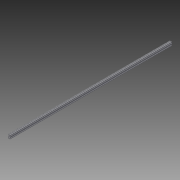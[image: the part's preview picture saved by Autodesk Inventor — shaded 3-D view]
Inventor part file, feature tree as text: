
AUTODESK INVENTOR PART (.ipt)
format: ipt  version: 2013 (Build 170138000, 138)  size: 219,648 bytes
history: native  units: in
note: dims shown in document units (in); Inventor stores cm internally (conversion verified against a paired STEP export)
features: extrude x1, sketch x1
ambient origin geometry x8: Origin, YZ Plane, XZ Plane, XY Plane, X Axis, Y Axis, Z Axis, Center Point
bodies: Solid1 (feature_tree)
feature tree (2):
  extrude  "Extrusion1"  [1 undecoded]
  sketch  "Sketch1"  dims[d0=70.8661in d1=0.0in]
note: 1 required parameter value undecoded (feature->parameter linkage not recoverable at this tier; creation-order binding heuristic only, values carry confidence <= 0.55)
